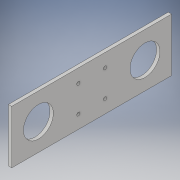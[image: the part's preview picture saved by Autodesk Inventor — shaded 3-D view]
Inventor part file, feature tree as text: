
AUTODESK INVENTOR PART (.ipt)
format: ipt  version: 2017 (Build 210142000, 142)  size: 109,568 bytes
history: native  units: in
note: dims shown in document units (in); Inventor stores cm internally (conversion verified against a paired STEP export)
features: extrude x1, sketch x1
ambient origin geometry x8: Origin, YZ Plane, XZ Plane, XY Plane, X Axis, Y Axis, Z Axis, Center Point
bodies: Body1 (feature_tree)
feature tree (2):
  extrude  "Extrusion2"  Depth=6.0in
  sketch  "Sketch1"  dims[d11=2.0in d12=6.0in d13=1.0in d14=1.125in d22=0.5in d23=0.5in d24=0.125in d25=0.125in d26=0.0in]
